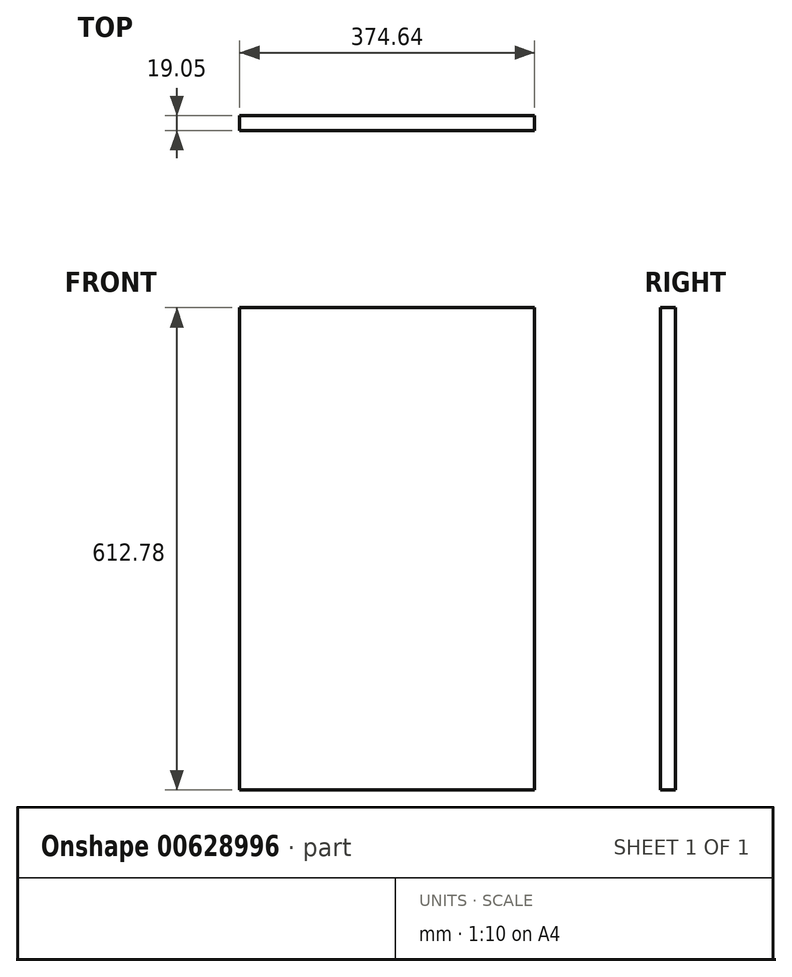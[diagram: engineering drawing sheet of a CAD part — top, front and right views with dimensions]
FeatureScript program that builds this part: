
annotation { "Feature Type Name" : "Feature", "Feature Type Description" : "" }
export const myFeature = defineFeature(function(context is Context, id is Id, definition is map)
    precondition{}
    {
        {
            var Q0;
            Q0=qCreatedBy(makeId("Front.planeOp"),FACE);
            var sketch = newSketch(context, id + "F0", { "sketchPlane" : qUnion([Q0])});
            skLineSegment(sketch, "E0.bottom", {"start": v(-187.32, 306.39) * mm, "end": v(187.33, 306.39) * mm});
            skLineSegment(sketch, "E0.top", {"start": v(-187.33, -306.39) * mm, "end": v(187.32, -306.39) * mm});
            skLineSegment(sketch, "E0.left", {"start": v(-187.32, 306.39) * mm, "end": v(-187.33, -306.39) * mm});
            skLineSegment(sketch, "E0.right", {"start": v(187.33, 306.39) * mm, "end": v(187.32, -306.39) * mm});
            skPoint(sketch, "E0.middle", {"position": v(0, 0) * mm});
            skSolve(sketch);
        }
        {
            var Q0;
            Q0=makeQuery(id+"F0.imprint","IMPRINT",FACE,{"disambiguationData":[TD([[makeQuery(id+"F0.imprint","IMPRINT",EDGE,{"derivedFrom":sQuery(id+"F0.wireOp",EDGE,"E0.bottom")}),-1.0]])]});
            extrude(context, id + "F1", {"entities" : qUnion([Q0]), "depth" : 19.05 * mm, "offsetDistance" : 25.4 * mm});
        }
    });
